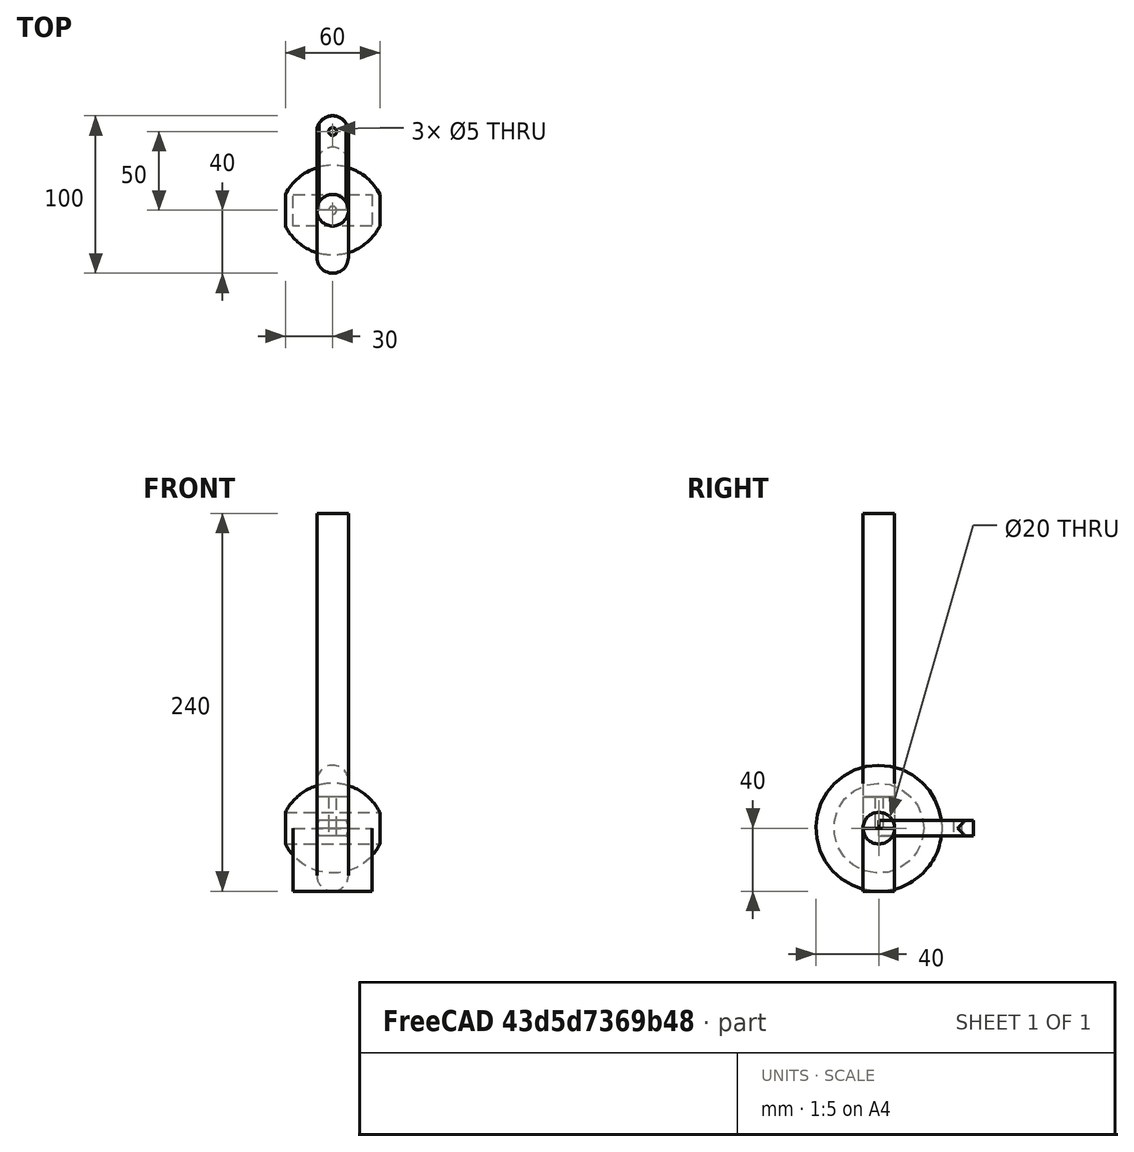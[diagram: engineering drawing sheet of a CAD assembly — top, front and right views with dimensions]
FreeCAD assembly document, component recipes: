
FREECAD ASSEMBLY — COMPONENT RECIPES ("Demo1Assembly")

This assembly document has 7 components, labeled P0..P6 below (a component is one placed body or linked part). 7 of them carry a construction recipe — the FreeCAD feature program that regenerates the part from scratch, quoted from this document or its linked companion documents; the rest are supplied as boundary geometry only. No exploded tour is included for this assembly.
COMPONENT P0 — recipe-attached ("Weight", modeled in this document).
Construction recipe (the document's own serialized feature program — sketch geometry with constraints, then the solid features built on it; lengths are millimeters unless a unit is written):

FEATURE [Sketcher::SketchObject] Sketch
  FullyConstrained = true
  MapMode = 5
  Support = -> [XY_Plane]
  sketch-geometry (2):
    g0: LineSegment StartX=-30 StartY=10 StartZ=0 EndX=30 EndY=10 EndZ=0
    g1: ArcOfCircle CenterX=0 CenterY=-5 CenterZ=0 NormalX=0 NormalY=0 NormalZ=1 AngleXU=0 Radius=33.541 StartAngle=0.463648 EndAngle=2.67795
  constraints (7):
    c: Horizontal(g0)
    c: DistanceY(g-1,g0) = 10
    c: DistanceX(g-1,g0) = 30
    c: PointOnObject(g1,g-2)
    c: DistanceY(g1,g-1) = 5
    c: Coincident(g1,g0)
    c: Coincident(g1,g0)
FEATURE [PartDesign::Revolution] Revolution
  Angle = 360
  Axis = (1,0,0)
  Base = (0,0,0)
  Profile = -> Sketch
  ReferenceAxis = -> Sketch [H_Axis]
FEATURE [PartDesign::CoordinateSystem] WeightTop
  AttacherType = Attacher::AttachEngine3D
  MapMode = 11
  Placement = pos=(30,-1.8e-15,0) rot=(0.707107,0,0.707107;3.14159rad)
  Support = -> [Revolution]
FEATURE [PartDesign::CoordinateSystem] WeightBot
  AttacherType = Attacher::AttachEngine3D
  MapMode = 11
  Placement = pos=(-30,0,0) rot=(0.707107,0,0.707107;3.14159rad)
  Support = -> [Revolution]
FEATURE [PartDesign::CoordinateSystem] WeightLCS
  AttacherType = Attacher::AttachEngine3D
  MapMode = 2
  Support = -> [Body003]
FEATURE [PartDesign::Body] Body  label="Weight"
  Group = -> [Sketch,Revolution,WeightLCS,WeightTop,WeightBot]
  Origin = -> Origin
  Tip = -> Revolution
COMPONENT P1 — recipe-attached ("Rod", modeled in this document).
Construction recipe (the document's own serialized feature program — sketch geometry with constraints, then the solid features built on it; lengths are millimeters unless a unit is written):

FEATURE [Sketcher::SketchObject] Sketch001
  FullyConstrained = true
  MapMode = 5
  Support = -> [XY_Plane001]
  sketch-geometry (1):
    g0: Circle CenterX=0 CenterY=0 CenterZ=0 NormalX=0 NormalY=0 NormalZ=1 AngleXU=0 Radius=10
  constraints (2):
    c: Coincident(g0,g-1)
    c: Diameter(g0) = 20
FEATURE [PartDesign::Pad] Pad
  Direction = (0,0,1)
  Length = 200
  Length2 = 10
  Profile = -> Sketch001
  ReferenceAxis = -> Sketch001 [N_Axis]
  Type = 0
FEATURE [PartDesign::CoordinateSystem] RodTop
  AttacherType = Attacher::AttachEngine3D
  MapMode = 11
  Placement = pos=(0,0,200) rot=(0,0,1;1.5708rad)
  Support = -> [Pad]
FEATURE [PartDesign::CoordinateSystem] RodBottom
  AttacherType = Attacher::AttachEngine3D
  MapMode = 11
  Placement = pos=(0,0,0) rot=(0,0,1;1.5708rad)
  Support = -> [Pad]
FEATURE [PartDesign::Body] Body001  label="Rod"
  Group = -> [Sketch001,Pad,RodTop,RodBottom]
  Origin = -> Origin001
  Tip = -> Pad
COMPONENT P2 — recipe-attached ("LugBody", modeled in this document).
Construction recipe (the document's own serialized feature program — sketch geometry with constraints, then the solid features built on it; lengths are millimeters unless a unit is written):

FEATURE [Sketcher::SketchObject] Sketch002
  FullyConstrained = true
  MapMode = 5
  Support = -> [XY_Plane002]
  sketch-geometry (5):
    g0: LineSegment StartX=-10 StartY=0 StartZ=0 EndX=-10 EndY=50 EndZ=0
    g1: ArcOfCircle CenterX=0 CenterY=50 CenterZ=0 NormalX=0 NormalY=0 NormalZ=1 AngleXU=0 Radius=10 StartAngle=1e-16 EndAngle=3.14159
    g2: LineSegment StartX=10 StartY=50 StartZ=0 EndX=10 EndY=0 EndZ=0
    g3: LineSegment StartX=10 StartY=0 StartZ=0 EndX=-10 EndY=0 EndZ=0
    g4: Circle CenterX=0 CenterY=50 CenterZ=0 NormalX=0 NormalY=0 NormalZ=1 AngleXU=0 Radius=2.5
  constraints (13):
    c: PointOnObject(g0,g-1)
    c: Vertical(g0)
    c: Tangent(g0,g1) = 1.5708
    c: Tangent(g1,g2) = 1.5708
    c: Coincident(g2,g3)
    c: Coincident(g3,g0)
    c: Horizontal(g3)
    c: PointOnObject(g1,g-2)
    c: Vertical(g2)
    c: Diameter(g1) = 20
    c: Distance(g2) = 50
    c: Coincident(g4,g1)
    c: Diameter(g4) = 5
FEATURE [PartDesign::Pad] Pad001
  Direction = (0,0,1)
  Length = 10
  Length2 = 10
  Midplane = true
  Profile = -> Sketch002
  ReferenceAxis = -> Sketch002 [N_Axis]
  Type = 0
FEATURE [PartDesign::Body] Body002  label="LugBody"
  Group = -> [Sketch002,Pad001]
  Origin = -> Origin002
  Tip = -> Pad001
COMPONENT P3 — recipe-attached ("LugCylinder", modeled in this document).
Construction recipe (the document's own serialized feature program — sketch geometry with constraints, then the solid features built on it; lengths are millimeters unless a unit is written):

FEATURE [Sketcher::SketchObject] Sketch003
  FullyConstrained = true
  MapMode = 5
  Placement = pos=(0,0,0) rot=(1,0,0;1.5708rad)
  Support = -> [XZ_Plane003]
  sketch-geometry (1):
    g0: Circle CenterX=0 CenterY=0 CenterZ=0 NormalX=0 NormalY=0 NormalZ=1 AngleXU=0 Radius=10
  constraints (2):
    c: Coincident(g0,g-1)
    c: Diameter(g0) = 20
FEATURE [PartDesign::Pad] Pad002
  Direction = (0,-1,-2e-16)
  Length = 60
  Length2 = 10
  Placement = pos=(0,0,0) rot=(1,0,0;1.5708rad)
  Profile = -> Sketch003
  ReferenceAxis = -> Sketch003 [N_Axis]
  Reversed = true
  Type = 0
FEATURE [PartDesign::Boolean] Boolean
  BaseFeature = -> Pad002
  Group = -> [Body002]
  Type = 2
FEATURE [PartDesign::CoordinateSystem] LugHole
  AttacherType = Attacher::AttachEngine3D
  MapMode = 11
  Placement = pos=(0,50,5) rot=(0,0,1;1.5708rad)
  Support = -> [Boolean]
FEATURE [PartDesign::CoordinateSystem] LugFace
  AttacherType = Attacher::AttachEngine3D
  MapMode = 5
  Placement = pos=(0,0,0) rot=(1,0,0;1.5708rad)
  Support = -> [Boolean]
FEATURE [PartDesign::CoordinateSystem] LugRot30
  AttacherType = Attacher::AttachEngine3D
  AttachmentOffset = pos=(0,0,0) rot=(0,0,1;0.523599rad)
  MapMode = 11
  Placement = pos=(0,50,5) rot=(0,0,1;2.0944rad)
  Support = -> [Boolean]
FEATURE [PartDesign::CoordinateSystem] LugRot60
  AttacherType = Attacher::AttachEngine3D
  AttachmentOffset = pos=(0,0,0) rot=(0,0,1;1.0472rad)
  MapMode = 11
  Placement = pos=(0,50,5) rot=(0,0,1;2.61799rad)
  Support = -> [Boolean]
FEATURE [PartDesign::Body] Body003  label="LugCylinder"
  Group = -> [Sketch003,Pad002,Boolean,LugHole,LugFace,LugRot30,LugRot60]
  Origin = -> Origin003
  Tip = -> Boolean
COMPONENT P4 — recipe-attached ("BobBody", modeled in this document).
Construction recipe (the document's own serialized feature program — sketch geometry with constraints, then the solid features built on it; lengths are millimeters unless a unit is written):

FEATURE [Sketcher::SketchObject] Sketch004
  FullyConstrained = true
  MapMode = 5
  Support = -> [XY_Plane004]
  sketch-geometry (4):
    g0: LineSegment StartX=-10 StartY=0 StartZ=0 EndX=-10 EndY=30 EndZ=0
    g1: ArcOfCircle CenterX=0 CenterY=30 CenterZ=0 NormalX=0 NormalY=0 NormalZ=1 AngleXU=0 Radius=10 StartAngle=2e-16 EndAngle=3.14159
    g2: LineSegment StartX=10 StartY=30 StartZ=0 EndX=10 EndY=0 EndZ=0
    g3: LineSegment StartX=10 StartY=0 StartZ=0 EndX=-10 EndY=0 EndZ=0
  constraints (11):
    c: PointOnObject(g0,g-1)
    c: Vertical(g0)
    c: Tangent(g0,g1) = 1.5708
    c: Tangent(g1,g2) = 1.5708
    c: Coincident(g2,g3)
    c: Coincident(g3,g0)
    c: Vertical(g2)
    c: PointOnObject(g1,g-2)
    c: Diameter(g1) = 20
    c: Distance(g0) = 30
    c: PointOnObject(g2,g-1)
FEATURE [PartDesign::Revolution] Revolution001
  Angle = 360
  Axis = (1,0,0)
  Base = (0,0,0)
  Profile = -> Sketch004
  ReferenceAxis = -> Sketch004 [H_Axis]
FEATURE [PartDesign::CoordinateSystem] BobBody  label="BobBody001"
  AttacherType = Attacher::AttachEngine3D
  MapMode = 11
  Placement = pos=(-10,0,0) rot=(0.707107,0,0.707107;3.14159rad)
  Support = -> [Revolution001]
FEATURE [PartDesign::Body] Body004  label="BobBody"
  Group = -> [Sketch004,Revolution001,BobBody]
  Origin = -> Origin004
  Tip = -> Revolution001
COMPONENT P5 — recipe-attached ("GroundBody", modeled in this document).
Construction recipe (the document's own serialized feature program — sketch geometry with constraints, then the solid features built on it; lengths are millimeters unless a unit is written):

FEATURE [Sketcher::SketchObject] Sketch005
  FullyConstrained = true
  MapMode = 5
  Support = -> [XY_Plane005]
  sketch-geometry (4):
    g0: LineSegment StartX=-25 StartY=10 StartZ=0 EndX=25 EndY=10 EndZ=0
    g1: LineSegment StartX=25 StartY=10 StartZ=0 EndX=25 EndY=-10 EndZ=0
    g2: LineSegment StartX=25 StartY=-10 StartZ=0 EndX=-25 EndY=-10 EndZ=0
    g3: LineSegment StartX=-25 StartY=-10 StartZ=0 EndX=-25 EndY=10 EndZ=0
  constraints (11):
    c: Coincident(g0,g1)
    c: Coincident(g1,g2)
    c: Coincident(g2,g3)
    c: Coincident(g3,g0)
    c: Horizontal(g0)
    c: Horizontal(g2)
    c: Vertical(g1)
    c: Vertical(g3)
    c: DistanceY(g2,g0) = 20
    c: DistanceX(g0,g0) = 50
    c: Symmetric(g0,g1,g-1)
FEATURE [PartDesign::Pad] Pad003
  Direction = (0,0,1)
  Length = 40
  Length2 = 10
  Profile = -> Sketch005
  ReferenceAxis = -> Sketch005 [N_Axis]
  Reversed = true
  Type = 0
FEATURE [PartDesign::CoordinateSystem] GroundLCS
  AttacherType = Attacher::AttachEngine3D
  MapMode = 5
  Placement = pos=(0,0,-40) rot=(1,0,0;3.14159rad)
  Support = -> [Pad003]
FEATURE [PartDesign::Body] Body005  label="GroundBody"
  Group = -> [Sketch005,Pad003,GroundLCS]
  Origin = -> Origin005
  Tip = -> Pad003
COMPONENT P6 — recipe-attached ("Spacer", modeled in this document).
Construction recipe (the document's own serialized feature program — sketch geometry with constraints, then the solid features built on it; lengths are millimeters unless a unit is written):

FEATURE [Sketcher::SketchObject] Sketch006
  FullyConstrained = true
  MapMode = 5
  Support = -> [XY_Plane007]
  sketch-geometry (2):
    g0: Circle CenterX=0 CenterY=0 CenterZ=0 NormalX=0 NormalY=0 NormalZ=1 AngleXU=0 Radius=10
    g1: Circle CenterX=0 CenterY=0 CenterZ=0 NormalX=0 NormalY=0 NormalZ=1 AngleXU=0 Radius=2.5
  constraints (4):
    c: Coincident(g0,g-1)
    c: Coincident(g1,g0)
    c: Diameter(g0) = 20
    c: Diameter(g1) = 5
FEATURE [PartDesign::Pad] Pad004
  Direction = (0,0,1)
  Length = 20
  Length2 = 10
  Profile = -> Sketch006
  ReferenceAxis = -> Sketch006 [N_Axis]
  Type = 0
FEATURE [PartDesign::CoordinateSystem] SpacerTop
  AttacherType = Attacher::AttachEngine3D
  MapMode = 11
  Placement = pos=(0,0,20) rot=(0,0,1;1.5708rad)
  Support = -> [Pad004]
FEATURE [PartDesign::Body] Body006  label="Spacer"
  Group = -> [Sketch006,Pad004,SpacerTop]
  Origin = -> Origin007
  Tip = -> Pad004
PROVENANCE & LICENSES
A FreeCAD (.FCStd) document from a public repository crawl; recipes are the document's own serialized feature recipes (and, for linked parts, companion documents' recipes).
License: gpl-3.0.
